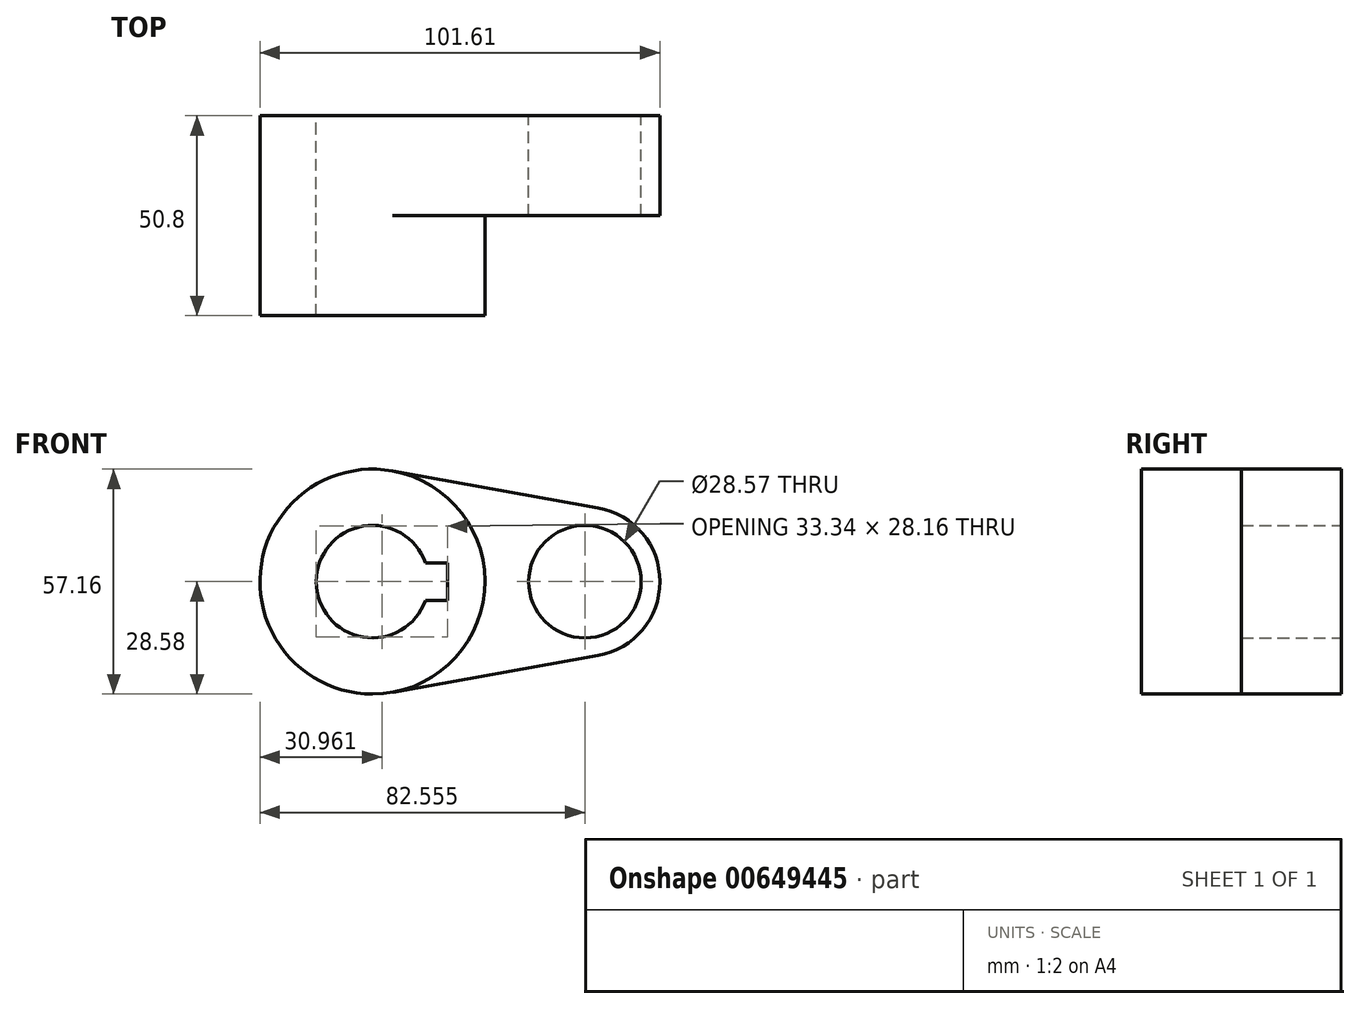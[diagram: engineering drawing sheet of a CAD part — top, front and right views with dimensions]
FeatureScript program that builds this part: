
annotation { "Feature Type Name" : "Feature", "Feature Type Description" : "" }
export const myFeature = defineFeature(function(context is Context, id is Id, definition is map)
    precondition{}
    {
        {
            var Q0;
            Q0=qCreatedBy(makeId("Front.planeOp"),FACE);
            var sketch = newSketch(context, id + "F0", { "sketchPlane" : qUnion([Q0])});
            skCircle(sketch, "E0", {"center": v(0, 0) * mm, "radius": 28.58 * mm});
            skCircle(sketch, "E1", {"center": v(0, 0) * mm, "radius": 14.29 * mm});
            skCircle(sketch, "E2", {"center": v(53.98, 0) * mm, "radius": 14.29 * mm});
            skCircle(sketch, "E3", {"center": v(53.98, 0) * mm, "radius": 19.05 * mm});
            skLineSegment(sketch, "E4", {"start": v(5.04, 28.13) * mm, "end": v(57.34, 18.75) * mm});
            skLineSegment(sketch, "E5", {"start": v(5.04, -28.13) * mm, "end": v(57.34, -18.75) * mm});
            skLineSegment(sketch, "E6.bottom", {"start": v(-19.05, -4.76) * mm, "end": v(19.05, -4.76) * mm});
            skLineSegment(sketch, "E6.top", {"start": v(-19.05, 4.76) * mm, "end": v(19.05, 4.76) * mm});
            skLineSegment(sketch, "E6.left", {"start": v(-19.05, -4.76) * mm, "end": v(-19.05, 4.76) * mm});
            skLineSegment(sketch, "E6.right", {"start": v(19.05, -4.76) * mm, "end": v(19.05, 4.76) * mm});
            skSolve(sketch);
        }
        {
            var Q0;
            {var subQ11=sQuery(id+"F0.wireOp",EDGE,"E6.left");Q0=makeQuery(id+"F0.imprint","IMPRINT",FACE,{"disambiguationData":[TD([[makeQuery(id+"F0.imprint","IMPRINT",EDGE,{"derivedFrom":subQ11}),1.0]])]});}
            var Q1;
            {var subQ0=sQuery(id+"F0.wireOp",EDGE,"E4");Q1=makeQuery(id+"F0.imprint","IMPRINT",FACE,{"disambiguationData":[TD([[makeQuery(id+"F0.imprint","IMPRINT",EDGE,{"derivedFrom":subQ0}),-1.0]])]});}
            var Q2;
            Q2=makeQuery(id+"F0.imprint","IMPRINT",FACE,{"disambiguationData":[TD([[makeQuery(id+"F0.imprint","IMPRINT",EDGE,{"derivedFrom":sQuery(id+"F0.wireOp",EDGE,"E2")}),-1.0]])]});
            var Q3;
            {var subQ5=sQuery(id+"F0.wireOp",EDGE,"E6.left");Q3=makeQuery(id+"F0.imprint","IMPRINT",FACE,{"disambiguationData":[TD([[makeQuery(id+"F0.imprint","IMPRINT",EDGE,{"derivedFrom":subQ5}),-1.0]])]});}
            extrude(context, id + "F1", {"entities" : qUnion([Q0, Q1, Q2, Q3]), "depth" : 25.4 * mm, "offsetDistance" : 25.4 * mm});
        }
        {
            var Q0;
            {var subQ11=sQuery(id+"F0.wireOp",EDGE,"E6.left");Q0=makeQuery(id+"F0.imprint","IMPRINT",FACE,{"disambiguationData":[TD([[makeQuery(id+"F0.imprint","IMPRINT",EDGE,{"derivedFrom":subQ11}),1.0]])]});}
            var Q1;
            {var subQ5=sQuery(id+"F0.wireOp",EDGE,"E6.left");Q1=makeQuery(id+"F0.imprint","IMPRINT",FACE,{"disambiguationData":[TD([[makeQuery(id+"F0.imprint","IMPRINT",EDGE,{"derivedFrom":subQ5}),-1.0]])]});}
            extrude(context, id + "F2", {"entities" : qUnion([Q0, Q1]), "operationType" : NewBodyOperationType.ADD, "depth" : 50.8 * mm, "offsetDistance" : 25.4 * mm});
        }
    });
